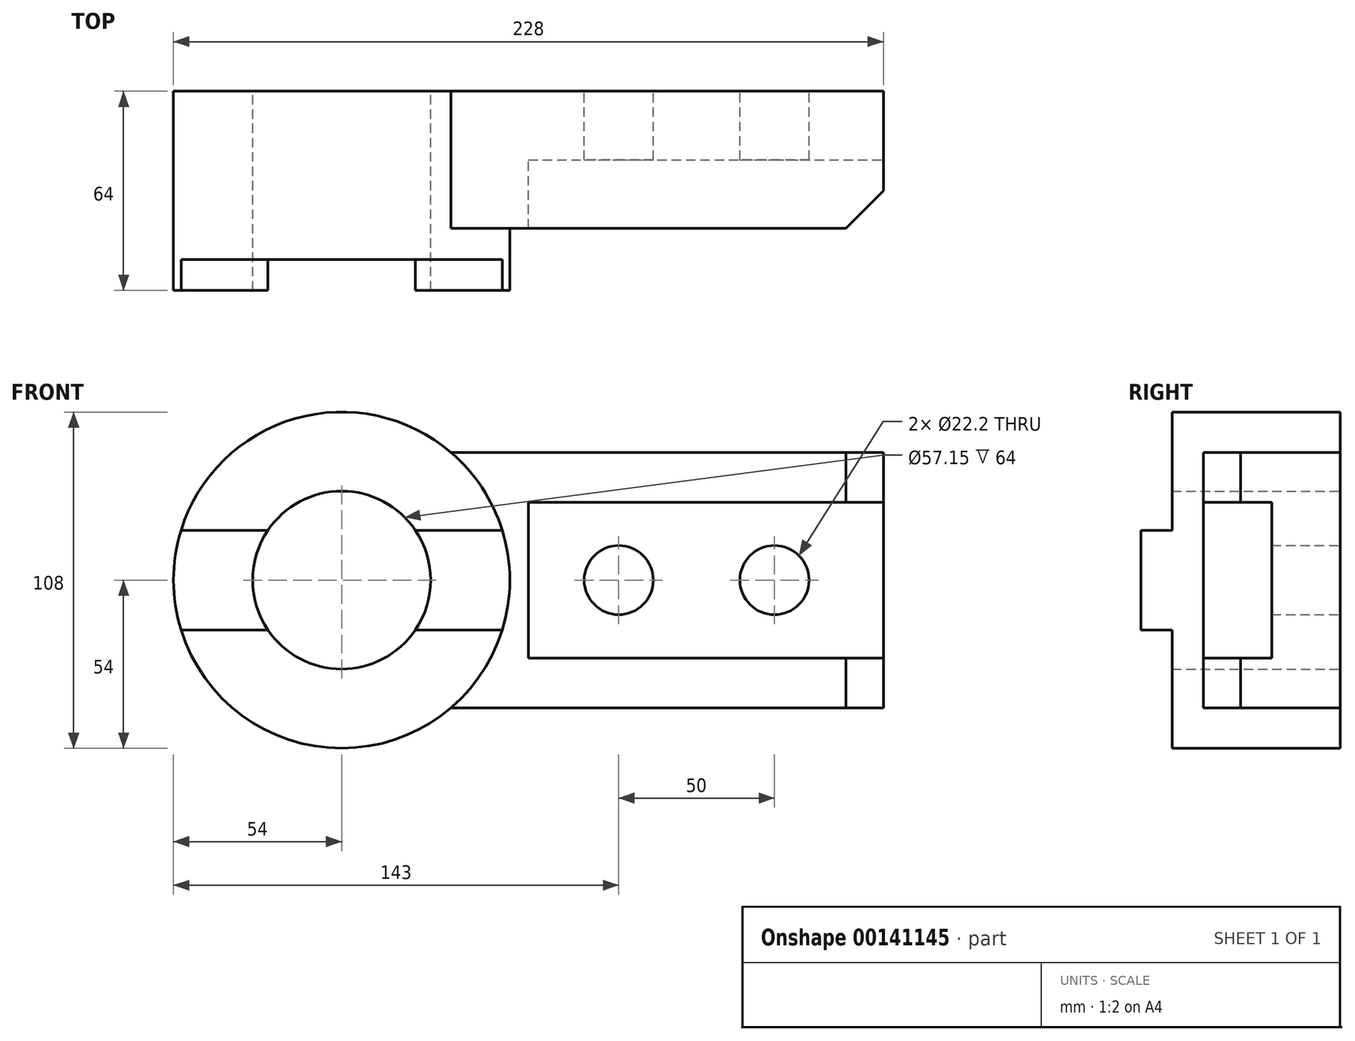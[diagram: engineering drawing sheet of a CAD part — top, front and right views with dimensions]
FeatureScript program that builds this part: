
annotation { "Feature Type Name" : "Feature", "Feature Type Description" : "" }
export const myFeature = defineFeature(function(context is Context, id is Id, definition is map)
    precondition{}
    {
        {
            var Q0;
            Q0=qCreatedBy(makeId("Front.planeOp"),FACE);
            var sketch = newSketch(context, id + "F0", { "sketchPlane" : qUnion([Q0])});
            skCircle(sketch, "E0", {"center": v(0, 0) * mm, "radius": 28.57 * mm});
            skCircle(sketch, "E1", {"center": v(0, 0) * mm, "radius": 54 * mm});
            skLineSegment(sketch, "E2", {"start": v(35.14, 41) * mm, "end": v(174, 41) * mm});
            skLineSegment(sketch, "E3", {"start": v(174, 41) * mm, "end": v(174, -41) * mm});
            skLineSegment(sketch, "E4", {"start": v(174, -41) * mm, "end": v(35.14, -41) * mm});
            skCircle(sketch, "E5", {"center": v(89, 0) * mm, "radius": 11.1 * mm});
            skCircle(sketch, "E6", {"center": v(139, 0) * mm, "radius": 11.1 * mm});
            skSolve(sketch);
        }
        {
            var Q0;
            Q0=makeQuery(id+"F0.imprint","IMPRINT",FACE,{"disambiguationData":[TD([[makeQuery(id+"F0.imprint","IMPRINT",EDGE,{"derivedFrom":sQuery(id+"F0.wireOp",EDGE,"E0")}),-1.0]])]});
            extrude(context, id + "F1", {"entities" : qUnion([Q0]), "depth" : 64 * mm});
        }
        {
            var Q0;
            {var subQ0=sQuery(id+"F0.wireOp",EDGE,"E2");Q0=makeQuery(id+"F0.imprint","IMPRINT",FACE,{"disambiguationData":[TD([[makeQuery(id+"F0.imprint","IMPRINT",EDGE,{"derivedFrom":subQ0}),-1.0]])]});}
            extrude(context, id + "F2", {"entities" : qUnion([Q0]), "operationType" : NewBodyOperationType.ADD, "depth" : 44 * mm});
        }
        {
            var Q0;
            Q0=qCreatedBy(makeId("Right.planeOp"),FACE);
            var sketch = newSketch(context, id + "F3", { "sketchPlane" : qUnion([Q0])});
            skLineSegment(sketch, "E7", {"start": v(-64, 54) * mm, "end": v(0, 54) * mm});
            skLineSegment(sketch, "E8", {"start": v(0, -54) * mm, "end": v(-64, -54) * mm});
            skLineSegment(sketch, "E9.0", {"start": v(-64, -54) * mm, "end": v(-64, 54) * mm});
            skLineSegment(sketch, "E10.bottom", {"start": v(-64, 54) * mm, "end": v(-54, 54) * mm});
            skLineSegment(sketch, "E10.top", {"start": v(-64, 16) * mm, "end": v(-54, 16) * mm});
            skLineSegment(sketch, "E10.left", {"start": v(-64, 54) * mm, "end": v(-64, 16) * mm});
            skLineSegment(sketch, "E10.right", {"start": v(-54, 54) * mm, "end": v(-54, 16) * mm});
            skLineSegment(sketch, "E11.bottom", {"start": v(-64, -54) * mm, "end": v(-54, -54) * mm});
            skLineSegment(sketch, "E11.top", {"start": v(-64, -16) * mm, "end": v(-54, -16) * mm});
            skLineSegment(sketch, "E11.left", {"start": v(-64, -54) * mm, "end": v(-64, -16) * mm});
            skLineSegment(sketch, "E11.right", {"start": v(-54, -54) * mm, "end": v(-54, -16) * mm});
            skSolve(sketch);
        }
        {
            var Q0;
            Q0 = qSketchRegion(id + "F3", true);
            extrude(context, id + "F4", {"entities" : qUnion([Q0]), "operationType" : NewBodyOperationType.REMOVE, "endBound" : BoundingType.SYMMETRIC, "oppositeDirection" : true, "depth" : 108 * mm});
        }
        {
            var Q0;
            Q0=makeQuery(id+"F2.opExtrude","SWEPT_FACE",FACE,{"disambiguationData":[OSD([sQuery(id+"F0.wireOp",EDGE,"E3")])]});
            cPlane(context, id + "F5", {"entities" : qUnion([Q0]), "cplaneType" : CPlaneType.OFFSET, "offset" : 0 * mm, "width" : 150 * mm, "height" : 150 * mm});
        }
        {
            var Q0;
            Q0=qCreatedBy(id+"F5.planeOp",FACE);
            var sketch = newSketch(context, id + "F6", { "sketchPlane" : qUnion([Q0])});
            skLineSegment(sketch, "E12.bottom", {"start": v(-44, 25) * mm, "end": v(-22, 25) * mm});
            skLineSegment(sketch, "E12.top", {"start": v(-44, -25) * mm, "end": v(-22, -25) * mm});
            skLineSegment(sketch, "E12.left", {"start": v(-44, 25) * mm, "end": v(-44, -25) * mm});
            skLineSegment(sketch, "E12.right", {"start": v(-22, 25) * mm, "end": v(-22, -25) * mm});
            skSolve(sketch);
        }
        {
            var Q0;
            Q0 = qSketchRegion(id + "F6", true);
            extrude(context, id + "F7", {"entities" : qUnion([Q0]), "operationType" : NewBodyOperationType.REMOVE, "oppositeDirection" : true, "depth" : 114 * mm});
        }
        {
            var Q0;
            Q0=qCreatedBy(makeId("Top.planeOp"),FACE);
            var sketch = newSketch(context, id + "F8", { "sketchPlane" : qUnion([Q0])});
            skLineSegment(sketch, "E13", {"start": v(162, -44) * mm, "end": v(174, -32) * mm});
            skLineSegment(sketch, "E14", {"start": v(174, -32) * mm, "end": v(174, -44) * mm});
            skLineSegment(sketch, "E15", {"start": v(174, -44) * mm, "end": v(162, -44) * mm});
            skSolve(sketch);
        }
        {
            var Q0;
            Q0 = qSketchRegion(id + "F8", true);
            extrude(context, id + "F9", {"entities" : qUnion([Q0]), "operationType" : NewBodyOperationType.REMOVE, "endBound" : BoundingType.SYMMETRIC, "oppositeDirection" : true, "depth" : 82 * mm});
        }
    });
